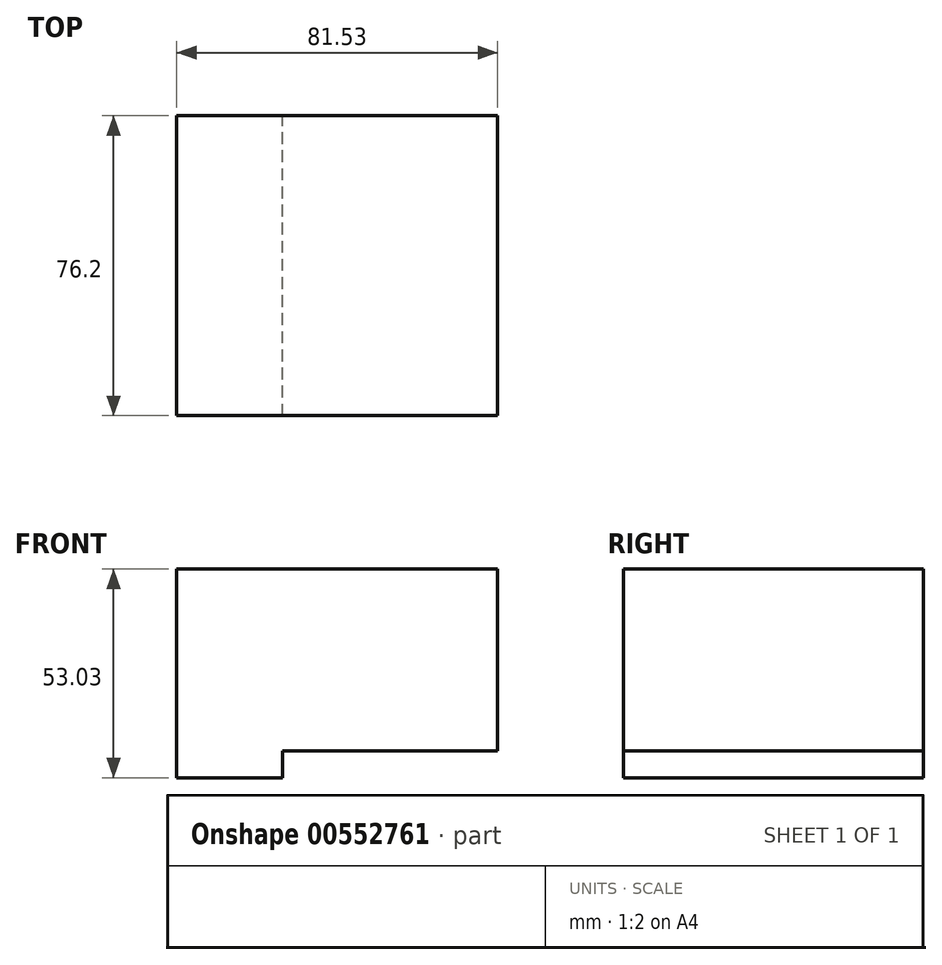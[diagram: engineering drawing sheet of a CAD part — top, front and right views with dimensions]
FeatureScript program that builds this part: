
annotation { "Feature Type Name" : "Feature", "Feature Type Description" : "" }
export const myFeature = defineFeature(function(context is Context, id is Id, definition is map)
    precondition{}
    {
        {
            var Q0;
            Q0=qCreatedBy(makeId("Front.planeOp"),FACE);
            var sketch = newSketch(context, id + "F0", { "sketchPlane" : qUnion([Q0])});
            skLineSegment(sketch, "E0.bottom", {"start": v(-100.54, 58.11) * mm, "end": v(-19, 58.11) * mm});
            skLineSegment(sketch, "E0.top", {"start": v(-100.54, 5.08) * mm, "end": v(-19, 5.08) * mm});
            skLineSegment(sketch, "E0.left", {"start": v(-100.54, 58.11) * mm, "end": v(-100.54, 5.08) * mm});
            skLineSegment(sketch, "E0.right", {"start": v(-19, 58.11) * mm, "end": v(-19, 5.08) * mm});
            skLineSegment(sketch, "E1.bottom", {"start": v(33.8, -3.76) * mm, "end": v(117.15, -3.76) * mm});
            skLineSegment(sketch, "E1.top", {"start": v(33.8, -55.5) * mm, "end": v(117.15, -55.5) * mm});
            skLineSegment(sketch, "E1.left", {"start": v(33.8, -3.76) * mm, "end": v(33.8, -55.5) * mm});
            skLineSegment(sketch, "E1.right", {"start": v(117.15, -3.76) * mm, "end": v(117.15, -55.5) * mm});
            skLineSegment(sketch, "E2.bottom", {"start": v(-73.71, 11.92) * mm, "end": v(45.33, 11.92) * mm});
            skLineSegment(sketch, "E2.top", {"start": v(-73.71, -29.39) * mm, "end": v(45.33, -29.39) * mm});
            skLineSegment(sketch, "E2.left", {"start": v(-73.71, 11.92) * mm, "end": v(-73.71, -29.39) * mm});
            skLineSegment(sketch, "E2.right", {"start": v(45.33, 11.92) * mm, "end": v(45.33, -29.39) * mm});
            skSolve(sketch);
        }
        {
            var Q0;
            {var subQ1=sQuery(id+"F0.wireOp",EDGE,"E0.bottom");Q0=makeQuery(id+"F0.imprint","IMPRINT",FACE,{"disambiguationData":[TD([[makeQuery(id+"F0.imprint","IMPRINT",EDGE,{"derivedFrom":subQ1}),-1.0]])]});}
            extrude(context, id + "F1", {"entities" : qUnion([Q0]), "depth" : 50.8 * mm, "offsetDistance" : 25.4 * mm, "hasSecondDirection" : true, "secondDirectionOppositeDirection" : true, "secondDirectionDepth" : 25.4 * mm});
        }
    });
